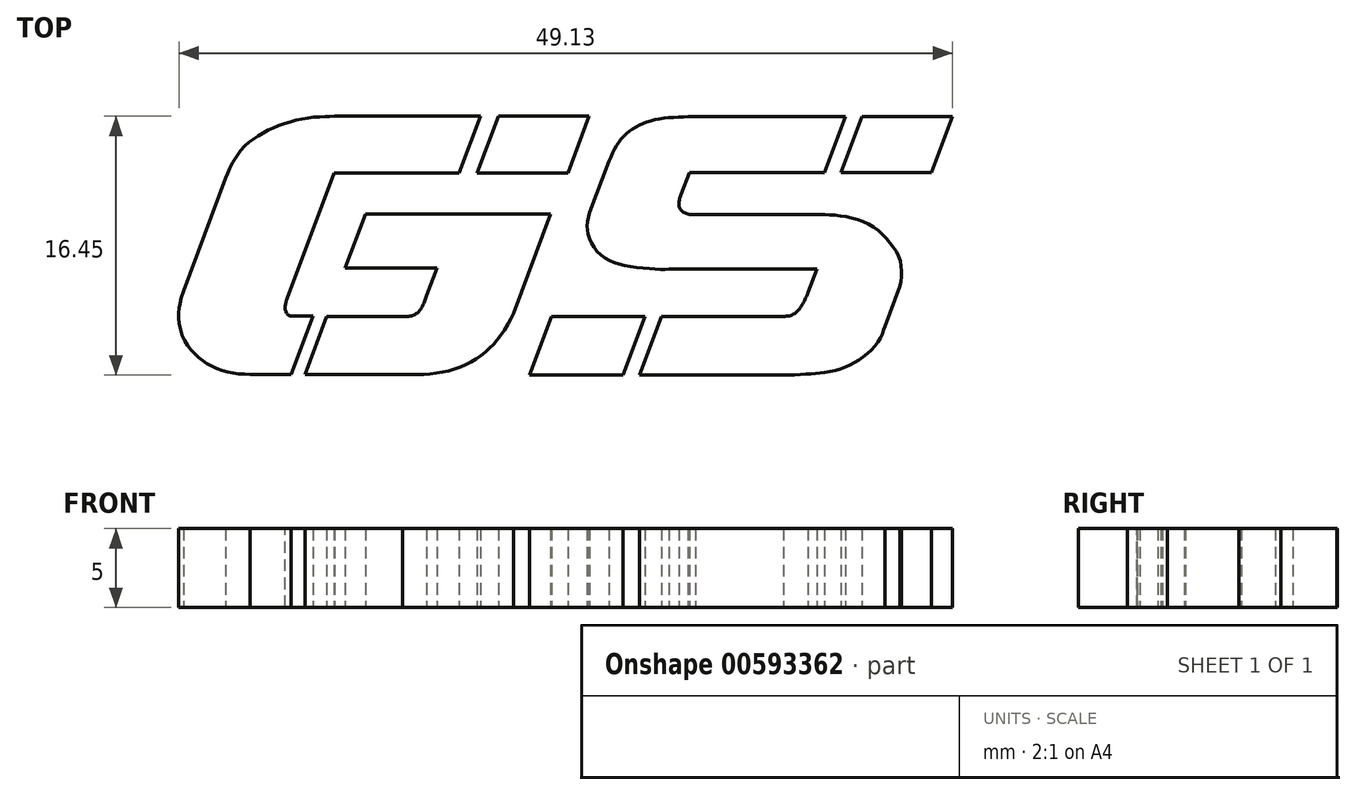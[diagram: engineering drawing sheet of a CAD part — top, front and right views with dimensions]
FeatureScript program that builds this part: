
annotation { "Feature Type Name" : "Feature", "Feature Type Description" : "" }
export const myFeature = defineFeature(function(context is Context, id is Id, definition is map)
    precondition{}
    {
        {
            var Q0;
            Q0=qCreatedBy(makeId("Top.planeOp"),FACE);
            var sketch = newSketch(context, id + "F0", { "sketchPlane" : qUnion([Q0])});
            skLineSegment(sketch, "E0", {"start": v(-9.84, 15.46) * mm, "end": v(1.68, 15.46) * mm});
            skLineSegment(sketch, "E1", {"start": v(1.68, 15.46) * mm, "end": v(-1.02, 8.24) * mm});
            skLineSegment(sketch, "E2", {"start": v(-1.02, 8.24) * mm, "end": v(-12.54, 8.24) * mm});
            skLineSegment(sketch, "E3", {"start": v(-12.54, 8.24) * mm, "end": v(-9.84, 15.46) * mm});
            skLineSegment(sketch, "E4", {"start": v(34.23, 15.39) * mm, "end": v(14.26, 15.39) * mm});
            skFitSpline(sketch, "E5", {"points": [v(14.26, 15.39) * mm, v(10.25, 15.05) * mm, v(7.57, 14.05) * mm, v(5.66, 12.47) * mm, v(4.2, 9.79) * mm], "startDerivative": vector(-14.04, -0.73) * mm, "endDerivative": vector(-5.32, -11.52) * mm});
            skLineSegment(sketch, "E6", {"start": v(4.2, 9.79) * mm, "end": v(1.75, 3.25) * mm});
            skFitSpline(sketch, "E7", {"points": [v(1.75, 3.25) * mm, v(1.41, 1.53) * mm, v(1.7, 0.05) * mm, v(2.7, -1.72) * mm, v(4.47, -2.96) * mm, v(6.86, -3.63) * mm, v(10.06, -3.97) * mm, v(11.83, -3.98) * mm], "startDerivative": vector(-3.67, -13.5) * mm, "endDerivative": vector(12.04, 0.33) * mm});
            skLineSegment(sketch, "E8", {"start": v(11.83, -3.98) * mm, "end": v(30.6, -3.98) * mm});
            skLineSegment(sketch, "E9", {"start": v(30.6, -3.98) * mm, "end": v(29.5, -6.93) * mm});
            skFitSpline(sketch, "E10", {"points": [v(29.5, -6.93) * mm, v(28.87, -8.25) * mm, v(28.23, -9.2) * mm, v(27.35, -9.82) * mm, v(26.34, -9.98) * mm], "startDerivative": vector(-2.9, -7.04) * mm, "endDerivative": vector(-4.91, -0.12) * mm});
            skLineSegment(sketch, "E11", {"start": v(26.34, -9.98) * mm, "end": v(10.87, -9.98) * mm});
            skLineSegment(sketch, "E12", {"start": v(10.87, -9.98) * mm, "end": v(8.05, -17.45) * mm});
            skLineSegment(sketch, "E13", {"start": v(8.05, -17.45) * mm, "end": v(27.04, -17.45) * mm});
            skFitSpline(sketch, "E14", {"points": [v(27.04, -17.45) * mm, v(29.61, -17.29) * mm, v(31.4, -17.12) * mm, v(33.77, -16.58) * mm, v(35.66, -15.67) * mm, v(37.59, -14.18) * mm, v(38.77, -12.56) * mm, v(39.27, -11.24) * mm], "startDerivative": vector(16.7, 0.03) * mm, "endDerivative": vector(4.6, 10.62) * mm});
            skLineSegment(sketch, "E15", {"start": v(39.27, -11.24) * mm, "end": v(41.18, -6.14) * mm});
            skFitSpline(sketch, "E16", {"points": [v(41.18, -6.14) * mm, v(41.36, -4.42) * mm, v(41.12, -2.66) * mm, v(40.28, -1.13) * mm, v(38.87, 0.52) * mm, v(37.02, 1.8) * mm, v(34.73, 2.6) * mm, v(32.64, 2.89) * mm, v(31, 2.95) * mm], "startDerivative": vector(4.07, 13.04) * mm, "endDerivative": vector(-14.03, 0.07) * mm});
            skLineSegment(sketch, "E17", {"start": v(31, 2.95) * mm, "end": v(15.2, 2.95) * mm});
            skFitSpline(sketch, "E18", {"points": [v(15.2, 2.95) * mm, v(13.91, 3.13) * mm, v(13.39, 3.49) * mm, v(13.12, 3.96) * mm, v(13.1, 4.64) * mm, v(13.36, 5.5) * mm], "startDerivative": vector(-6.9, -0.33) * mm, "endDerivative": vector(1.6, 4.23) * mm});
            skLineSegment(sketch, "E19", {"start": v(13.36, 5.5) * mm, "end": v(14.4, 8.27) * mm});
            skLineSegment(sketch, "E20", {"start": v(14.4, 8.27) * mm, "end": v(31.55, 8.27) * mm});
            skLineSegment(sketch, "E21", {"start": v(31.55, 8.27) * mm, "end": v(34.23, 15.39) * mm});
            skLineSegment(sketch, "E22", {"start": v(36.34, 15.39) * mm, "end": v(47.82, 15.39) * mm});
            skLineSegment(sketch, "E23", {"start": v(47.82, 15.39) * mm, "end": v(45.15, 8.27) * mm});
            skLineSegment(sketch, "E24", {"start": v(45.15, 8.27) * mm, "end": v(33.66, 8.27) * mm});
            skLineSegment(sketch, "E25", {"start": v(33.66, 8.27) * mm, "end": v(36.34, 15.39) * mm});
            skLineSegment(sketch, "E26", {"start": v(8.77, -9.98) * mm, "end": v(-3.07, -9.98) * mm});
            skLineSegment(sketch, "E27", {"start": v(-3.07, -9.98) * mm, "end": v(-5.89, -17.45) * mm});
            skLineSegment(sketch, "E28", {"start": v(-5.89, -17.45) * mm, "end": v(5.96, -17.45) * mm});
            skLineSegment(sketch, "E29", {"start": v(5.96, -17.45) * mm, "end": v(8.77, -9.98) * mm});
            skLineSegment(sketch, "E30", {"start": v(-26.73, 3.04) * mm, "end": v(-3.22, 3.04) * mm});
            skLineSegment(sketch, "E31", {"start": v(-3.22, 3.04) * mm, "end": v(-7.94, -9.62) * mm});
            skFitSpline(sketch, "E32", {"points": [v(-7.94, -9.62) * mm, v(-9.34, -12.07) * mm, v(-10.86, -13.9) * mm, v(-12.6, -15.33) * mm, v(-14.86, -16.47) * mm, v(-17.45, -17.16) * mm, v(-20.08, -17.38) * mm, v(-22.02, -17.36) * mm], "startDerivative": vector(-5.6, -13.2) * mm, "endDerivative": vector(-15.76, 0.23) * mm});
            skLineSegment(sketch, "E33", {"start": v(-22.02, -17.36) * mm, "end": v(-34.4, -17.36) * mm});
            skLineSegment(sketch, "E34", {"start": v(-34.4, -17.36) * mm, "end": v(-31.65, -10) * mm});
            skLineSegment(sketch, "E35", {"start": v(-31.65, -10) * mm, "end": v(-22.02, -10) * mm});
            skFitSpline(sketch, "E36", {"points": [v(-22.02, -10) * mm, v(-20.87, -9.9) * mm, v(-20.24, -9.6) * mm, v(-19.68, -8.99) * mm, v(-19.31, -8.25) * mm, v(-18.97, -7.33) * mm], "startDerivative": vector(6.7, -0.01) * mm, "endDerivative": vector(1.5, 4.1) * mm});
            skLineSegment(sketch, "E37", {"start": v(-18.97, -7.33) * mm, "end": v(-17.65, -3.85) * mm});
            skLineSegment(sketch, "E38", {"start": v(-17.65, -3.85) * mm, "end": v(-29.3, -3.85) * mm});
            skLineSegment(sketch, "E39", {"start": v(-29.3, -3.85) * mm, "end": v(-26.73, 3.04) * mm});
            skLineSegment(sketch, "E40", {"start": v(-12.14, 15.46) * mm, "end": v(-14.83, 8.24) * mm});
            skLineSegment(sketch, "E41", {"start": v(-14.83, 8.24) * mm, "end": v(-30.72, 8.24) * mm});
            skLineSegment(sketch, "E42", {"start": v(-30.72, 8.24) * mm, "end": v(-36.69, -7.73) * mm});
            skFitSpline(sketch, "E43", {"points": [v(-36.69, -7.73) * mm, v(-36.87, -8.32) * mm, v(-36.94, -8.8) * mm, v(-36.86, -9.33) * mm, v(-36.67, -9.66) * mm, v(-36.37, -9.88) * mm, v(-36, -9.96) * mm, v(-35.52, -9.95) * mm], "startDerivative": vector(-1.21, -3.2) * mm, "endDerivative": vector(2.58, -0.02) * mm});
            skLineSegment(sketch, "E44", {"start": v(-35.52, -9.95) * mm, "end": v(-33.42, -9.95) * mm});
            skLineSegment(sketch, "E45", {"start": v(-33.42, -9.95) * mm, "end": v(-36.18, -17.36) * mm});
            skLineSegment(sketch, "E46", {"start": v(-36.18, -17.36) * mm, "end": v(-41.39, -17.36) * mm});
            skFitSpline(sketch, "E47", {"points": [v(-41.39, -17.36) * mm, v(-43.31, -17.22) * mm, v(-45.14, -16.78) * mm, v(-46.78, -16.02) * mm, v(-47.98, -15.15) * mm, v(-49.16, -13.9) * mm, v(-50.09, -12.2) * mm, v(-50.44, -10.19) * mm, v(-50.37, -8.8) * mm, v(-49.84, -6.74) * mm], "startDerivative": vector(-16.88, 0.83) * mm, "endDerivative": vector(8.25, 23.17) * mm});
            skLineSegment(sketch, "E48", {"start": v(-49.84, -6.74) * mm, "end": v(-44.5, 7.57) * mm});
            skFitSpline(sketch, "E49", {"points": [v(-44.5, 7.57) * mm, v(-43.95, 8.9) * mm, v(-42.67, 11) * mm, v(-41.37, 12.27) * mm, v(-40.05, 13.14) * mm, v(-38.63, 13.9) * mm, v(-36.94, 14.53) * mm, v(-35.12, 15.04) * mm, v(-33.38, 15.31) * mm, v(-31.74, 15.4) * mm, v(-30.67, 15.46) * mm], "startDerivative": vector(6.03, 15.28) * mm, "endDerivative": vector(16.5, 0.42) * mm});
            skLineSegment(sketch, "E50", {"start": v(-30.67, 15.46) * mm, "end": v(-12.14, 15.46) * mm});
            skSolve(sketch);
        }
        {
            var Q0;
            Q0=qSketchRegion(id+"F0",true);
            extrude(context, id + "F1", {"entities" : qUnion([Q0]), "depth" : 10 * mm, "offsetDistance" : 25 * mm});
        }
        {
            var Q0;
            Q0=makeQuery(id+"F1.opExtrude","SWEPT_BODY",BODY,{"disambiguationData":[OSD([sQuery(id+"F0.wireOp",EDGE,"E40"),sQuery(id+"F0.wireOp",EDGE,"E41"),sQuery(id+"F0.wireOp",EDGE,"E42"),sQuery(id+"F0.wireOp",EDGE,"E43"),sQuery(id+"F0.wireOp",EDGE,"E44"),sQuery(id+"F0.wireOp",EDGE,"E45"),sQuery(id+"F0.wireOp",EDGE,"E46"),sQuery(id+"F0.wireOp",EDGE,"E47"),sQuery(id+"F0.wireOp",EDGE,"E48"),sQuery(id+"F0.wireOp",EDGE,"E49"),sQuery(id+"F0.wireOp",EDGE,"E50")])]});
            var Q1;
            Q1=makeQuery(id+"F1.opExtrude","SWEPT_BODY",BODY,{"disambiguationData":[OSD([sQuery(id+"F0.wireOp",EDGE,"E30"),sQuery(id+"F0.wireOp",EDGE,"E31"),sQuery(id+"F0.wireOp",EDGE,"E32"),sQuery(id+"F0.wireOp",EDGE,"E33"),sQuery(id+"F0.wireOp",EDGE,"E34"),sQuery(id+"F0.wireOp",EDGE,"E35"),sQuery(id+"F0.wireOp",EDGE,"E36"),sQuery(id+"F0.wireOp",EDGE,"E37"),sQuery(id+"F0.wireOp",EDGE,"E38"),sQuery(id+"F0.wireOp",EDGE,"E39")])]});
            var Q2;
            Q2=makeQuery(id+"F1.opExtrude","SWEPT_BODY",BODY,{"disambiguationData":[OSD([sQuery(id+"F0.wireOp",EDGE,"E0"),sQuery(id+"F0.wireOp",EDGE,"E1"),sQuery(id+"F0.wireOp",EDGE,"E2"),sQuery(id+"F0.wireOp",EDGE,"E3")])]});
            var Q3;
            Q3=makeQuery(id+"F1.opExtrude","SWEPT_BODY",BODY,{"disambiguationData":[OSD([sQuery(id+"F0.wireOp",EDGE,"E4"),sQuery(id+"F0.wireOp",EDGE,"E5"),sQuery(id+"F0.wireOp",EDGE,"E6"),sQuery(id+"F0.wireOp",EDGE,"E7"),sQuery(id+"F0.wireOp",EDGE,"E8"),sQuery(id+"F0.wireOp",EDGE,"E9"),sQuery(id+"F0.wireOp",EDGE,"E10"),sQuery(id+"F0.wireOp",EDGE,"E11"),sQuery(id+"F0.wireOp",EDGE,"E12"),sQuery(id+"F0.wireOp",EDGE,"E13"),sQuery(id+"F0.wireOp",EDGE,"E14"),sQuery(id+"F0.wireOp",EDGE,"E15"),sQuery(id+"F0.wireOp",EDGE,"E16"),sQuery(id+"F0.wireOp",EDGE,"E17"),sQuery(id+"F0.wireOp",EDGE,"E18"),sQuery(id+"F0.wireOp",EDGE,"E19"),sQuery(id+"F0.wireOp",EDGE,"E20"),sQuery(id+"F0.wireOp",EDGE,"E21")])]});
            var Q4;
            Q4=makeQuery(id+"F1.opExtrude","SWEPT_BODY",BODY,{"disambiguationData":[OSD([sQuery(id+"F0.wireOp",EDGE,"E22"),sQuery(id+"F0.wireOp",EDGE,"E23"),sQuery(id+"F0.wireOp",EDGE,"E24"),sQuery(id+"F0.wireOp",EDGE,"E25")])]});
            var Q5;
            Q5=makeQuery(id+"F1.opExtrude","SWEPT_BODY",BODY,{"disambiguationData":[OSD([sQuery(id+"F0.wireOp",EDGE,"E26"),sQuery(id+"F0.wireOp",EDGE,"E27"),sQuery(id+"F0.wireOp",EDGE,"E28"),sQuery(id+"F0.wireOp",EDGE,"E29")])]});
            var Q6;
            Q6=qCreatedBy(makeId("Origin.pointOp"),VERTEX);
            transform(context, id + "F2", {"entities" : qUnion([Q0, Q1, Q2, Q3, Q4, Q5]), "transformType" : TransformType.SCALE_UNIFORMLY, "scale" : 0.5, "scalePoint" : qUnion([Q6]), "makeCopy" : false});
        }
        {
            var Q0;
            Q0=makeQuery(id+"F1.opExtrude","SWEPT_BODY",BODY,{"disambiguationData":[OSD([sQuery(id+"F0.wireOp",EDGE,"E40"),sQuery(id+"F0.wireOp",EDGE,"E41"),sQuery(id+"F0.wireOp",EDGE,"E42"),sQuery(id+"F0.wireOp",EDGE,"E43"),sQuery(id+"F0.wireOp",EDGE,"E44"),sQuery(id+"F0.wireOp",EDGE,"E45"),sQuery(id+"F0.wireOp",EDGE,"E46"),sQuery(id+"F0.wireOp",EDGE,"E47"),sQuery(id+"F0.wireOp",EDGE,"E48"),sQuery(id+"F0.wireOp",EDGE,"E49"),sQuery(id+"F0.wireOp",EDGE,"E50")])]});
            var Q1;
            Q1=makeQuery(id+"F1.opExtrude","SWEPT_BODY",BODY,{"disambiguationData":[OSD([sQuery(id+"F0.wireOp",EDGE,"E30"),sQuery(id+"F0.wireOp",EDGE,"E31"),sQuery(id+"F0.wireOp",EDGE,"E32"),sQuery(id+"F0.wireOp",EDGE,"E33"),sQuery(id+"F0.wireOp",EDGE,"E34"),sQuery(id+"F0.wireOp",EDGE,"E35"),sQuery(id+"F0.wireOp",EDGE,"E36"),sQuery(id+"F0.wireOp",EDGE,"E37"),sQuery(id+"F0.wireOp",EDGE,"E38"),sQuery(id+"F0.wireOp",EDGE,"E39")])]});
            var Q2;
            Q2=makeQuery(id+"F1.opExtrude","SWEPT_BODY",BODY,{"disambiguationData":[OSD([sQuery(id+"F0.wireOp",EDGE,"E0"),sQuery(id+"F0.wireOp",EDGE,"E1"),sQuery(id+"F0.wireOp",EDGE,"E2"),sQuery(id+"F0.wireOp",EDGE,"E3")])]});
            var Q3;
            Q3=makeQuery(id+"F1.opExtrude","SWEPT_BODY",BODY,{"disambiguationData":[OSD([sQuery(id+"F0.wireOp",EDGE,"E4"),sQuery(id+"F0.wireOp",EDGE,"E5"),sQuery(id+"F0.wireOp",EDGE,"E6"),sQuery(id+"F0.wireOp",EDGE,"E7"),sQuery(id+"F0.wireOp",EDGE,"E8"),sQuery(id+"F0.wireOp",EDGE,"E9"),sQuery(id+"F0.wireOp",EDGE,"E10"),sQuery(id+"F0.wireOp",EDGE,"E11"),sQuery(id+"F0.wireOp",EDGE,"E12"),sQuery(id+"F0.wireOp",EDGE,"E13"),sQuery(id+"F0.wireOp",EDGE,"E14"),sQuery(id+"F0.wireOp",EDGE,"E15"),sQuery(id+"F0.wireOp",EDGE,"E16"),sQuery(id+"F0.wireOp",EDGE,"E17"),sQuery(id+"F0.wireOp",EDGE,"E18"),sQuery(id+"F0.wireOp",EDGE,"E19"),sQuery(id+"F0.wireOp",EDGE,"E20"),sQuery(id+"F0.wireOp",EDGE,"E21")])]});
            var Q4;
            Q4=makeQuery(id+"F1.opExtrude","SWEPT_BODY",BODY,{"disambiguationData":[OSD([sQuery(id+"F0.wireOp",EDGE,"E22"),sQuery(id+"F0.wireOp",EDGE,"E23"),sQuery(id+"F0.wireOp",EDGE,"E24"),sQuery(id+"F0.wireOp",EDGE,"E25")])]});
            var Q5;
            Q5=makeQuery(id+"F1.opExtrude","SWEPT_BODY",BODY,{"disambiguationData":[OSD([sQuery(id+"F0.wireOp",EDGE,"E26"),sQuery(id+"F0.wireOp",EDGE,"E27"),sQuery(id+"F0.wireOp",EDGE,"E28"),sQuery(id+"F0.wireOp",EDGE,"E29")])]});
            var Q6;
            Q6=qCreatedBy(makeId("Top.planeOp"),FACE);
            transform(context, id + "F3", {"entities" : qUnion([Q0, Q1, Q2, Q3, Q4, Q5]), "transformType" : TransformType.TRANSLATION_DISTANCE, "transformDirection" : qUnion([Q6]), "distance" : 3 * mm, "makeCopy" : false});
        }
    });
